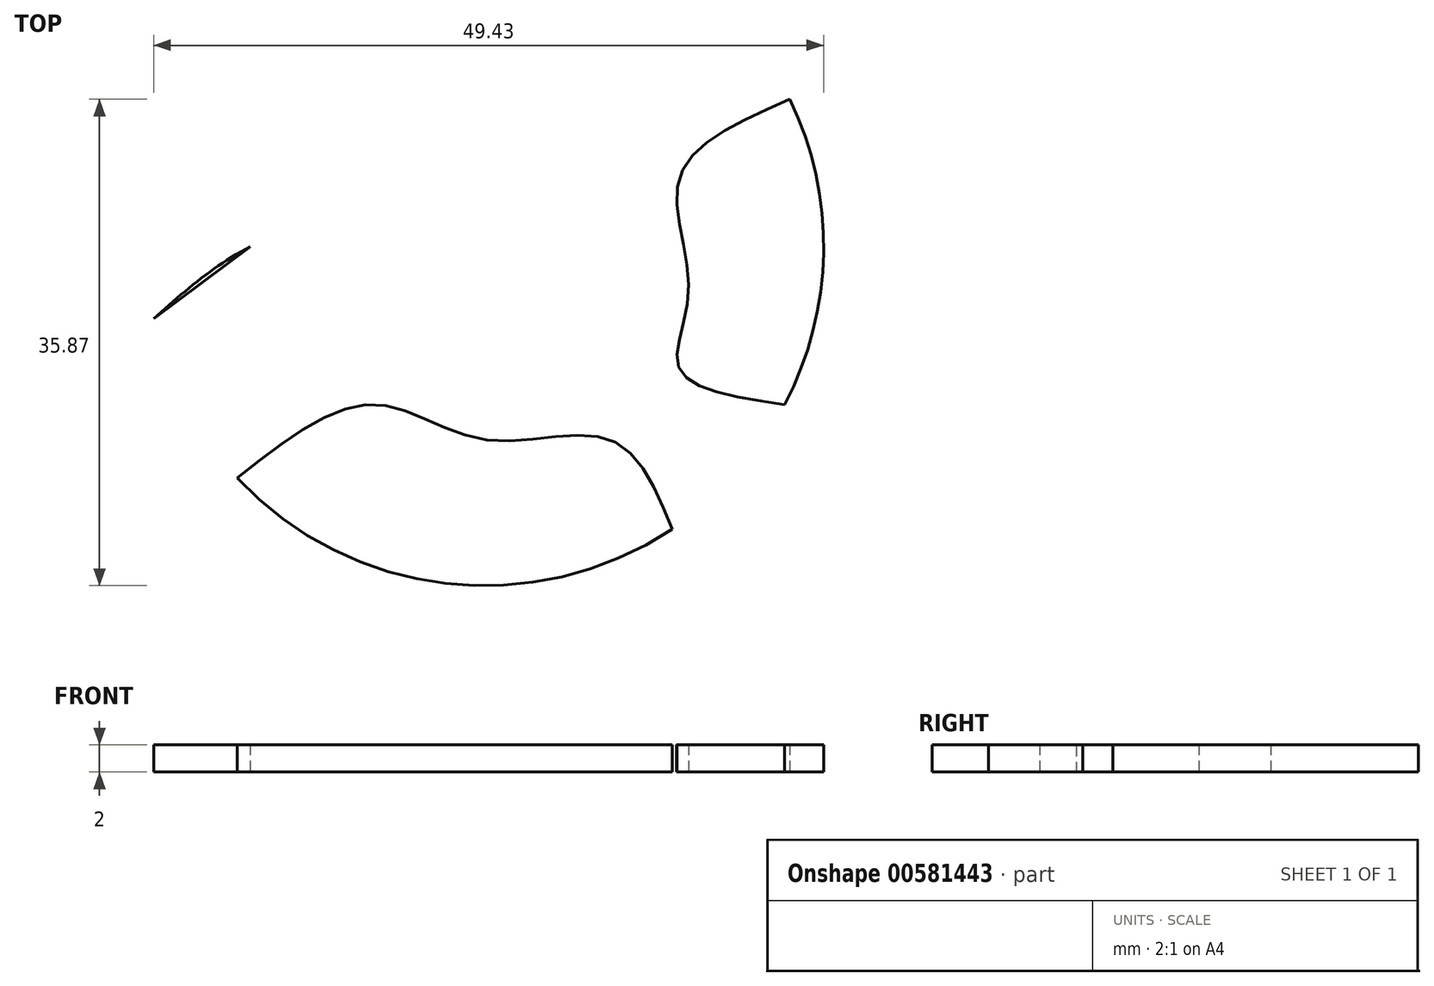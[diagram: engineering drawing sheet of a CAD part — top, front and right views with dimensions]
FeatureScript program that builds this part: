
annotation { "Feature Type Name" : "Feature", "Feature Type Description" : "" }
export const myFeature = defineFeature(function(context is Context, id is Id, definition is map)
    precondition{}
    {
        {
            var Q0;
            Q0=qCreatedBy(makeId("Top.planeOp"),FACE);
            var sketch = newSketch(context, id + "F0", { "sketchPlane" : qUnion([Q0])});
            skCircle(sketch, "E0", {"center": v(0, 0) * mm, "radius": 25 * mm});
            skLineSegment(sketch, "E1", {"start": v(-24.43, -5.32) * mm, "end": v(-17.3, 0) * mm});
            skLineSegment(sketch, "E2", {"start": v(0, 16.82) * mm, "end": v(0, 12.29) * mm});
            skFitSpline(sketch, "E3", {"points": [v(-24.43, -5.32) * mm, v(-17.3, 0) * mm, v(-6.95, 4.53) * mm, v(0, 12.29) * mm, v(0, 16.82) * mm], "startDerivative": vector(25.68, 23.1) * mm, "endDerivative": vector(-4.7, 23.42) * mm});
            skFitSpline(sketch, "E4", {"points": [v(0, 16.82) * mm, v(5.98, 21.34) * mm, v(12.35, 21.74) * mm], "startDerivative": vector(11.04, 10.75) * mm, "endDerivative": vector(13.68, -1.08) * mm});
            skFitSpline(sketch, "E5", {"points": [v(22.51, 10.87) * mm, v(14.4, 5.17) * mm, v(15.04, -3.23) * mm, v(14.4, -9.06) * mm, v(22.12, -11.65) * mm], "startDerivative": vector(-39.1, -16.9) * mm, "endDerivative": vector(41.16, -6) * mm});
            skFitSpline(sketch, "E6", {"points": [v(-18.27, -17.06) * mm, v(-8.25, -11.64) * mm, v(0, -14.23) * mm, v(9.22, -14.23) * mm, v(13.83, -20.83) * mm], "startDerivative": vector(37.27, 29.47) * mm, "endDerivative": vector(15.08, -36.88) * mm});
            skSolve(sketch);
        }
        {
            var Q0;
            {var subQ1=sQuery(id+"F0.wireOp",EDGE,"E1");Q0=makeQuery(id+"F0.imprint","IMPRINT",FACE,{"disambiguationData":[TD([[makeQuery(id+"F0.imprint","IMPRINT",EDGE,{"derivedFrom":subQ1}),1.0]])]});}
            var Q1;
            {var subQ0=sQuery(id+"F0.wireOp",EDGE,"E5");Q1=makeQuery(id+"F0.imprint","IMPRINT",FACE,{"disambiguationData":[TD([[makeQuery(id+"F0.imprint","IMPRINT",EDGE,{"derivedFrom":subQ0}),1.0]])]});}
            var Q2;
            {var subQ0=sQuery(id+"F0.wireOp",EDGE,"E6");Q2=makeQuery(id+"F0.imprint","IMPRINT",FACE,{"disambiguationData":[TD([[makeQuery(id+"F0.imprint","IMPRINT",EDGE,{"derivedFrom":subQ0}),-1.0]])]});}
            extrude(context, id + "F1", {"entities" : qUnion([Q0, Q1, Q2]), "depth" : 2 * mm, "offsetDistance" : 25 * mm});
        }
    });
